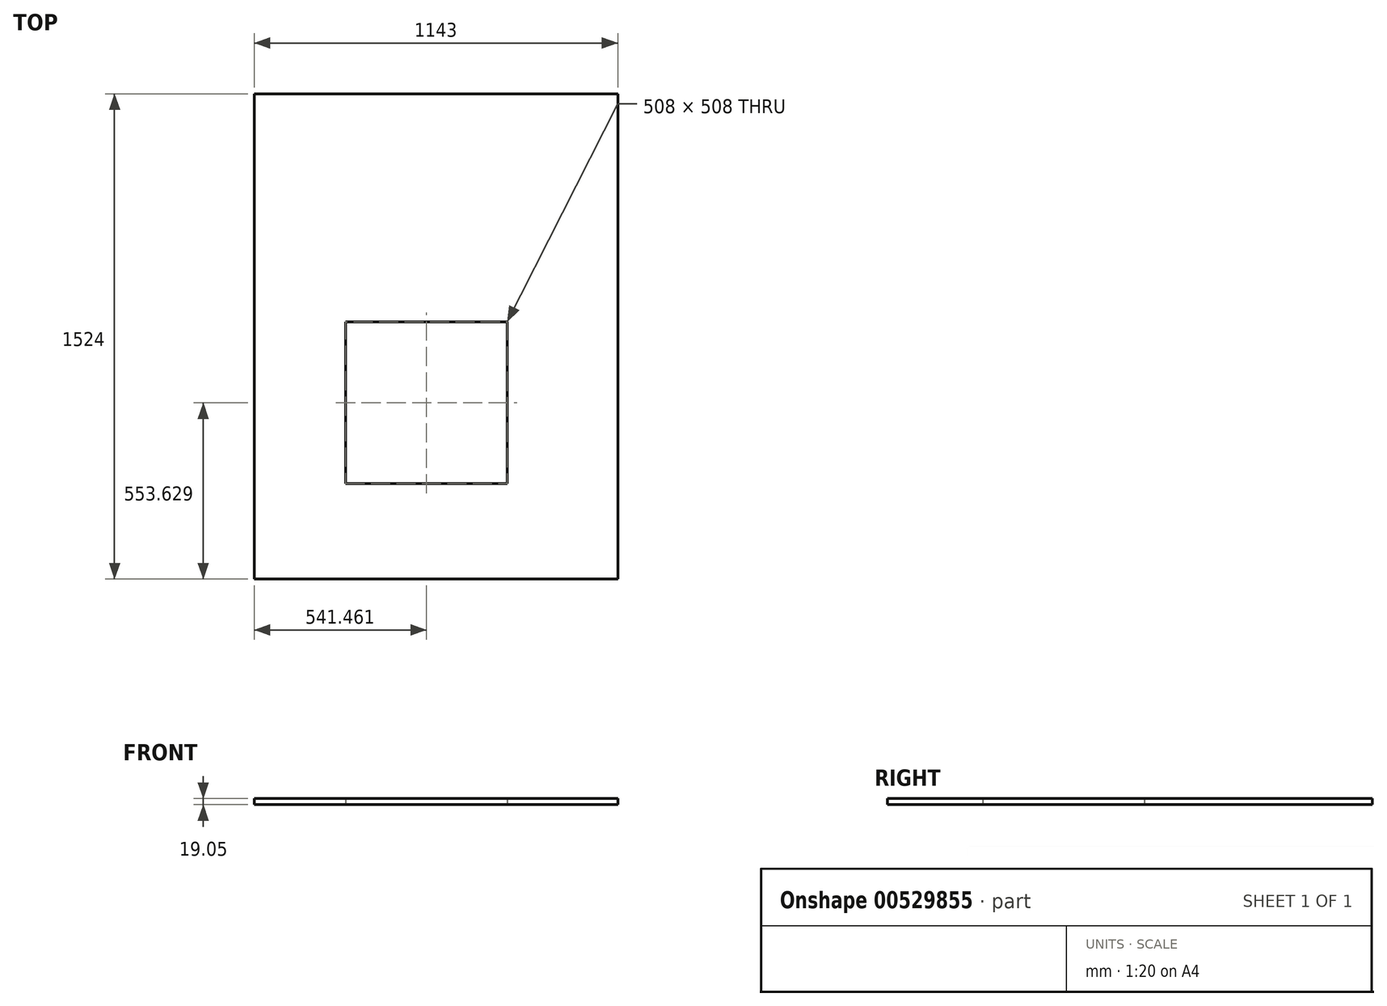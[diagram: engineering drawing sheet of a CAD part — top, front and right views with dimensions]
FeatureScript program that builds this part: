
annotation { "Feature Type Name" : "Feature", "Feature Type Description" : "" }
export const myFeature = defineFeature(function(context is Context, id is Id, definition is map)
    precondition{}
    {
        {
            var Q0;
            Q0=qCreatedBy(makeId("Top.planeOp"),FACE);
            var sketch = newSketch(context, id + "F0", { "sketchPlane" : qUnion([Q0])});
            skLineSegment(sketch, "E0.bottom", {"start": v(-571.59, 1082.27) * mm, "end": v(571.41, 1082.27) * mm});
            skLineSegment(sketch, "E0.top", {"start": v(-571.59, -441.73) * mm, "end": v(571.41, -441.73) * mm});
            skLineSegment(sketch, "E0.left", {"start": v(-571.59, 1082.27) * mm, "end": v(-571.59, -441.73) * mm});
            skLineSegment(sketch, "E0.right", {"start": v(571.41, 1082.27) * mm, "end": v(571.41, -441.73) * mm});
            skLineSegment(sketch, "E1.bottom", {"start": v(-284.13, 365.9) * mm, "end": v(223.87, 365.9) * mm});
            skLineSegment(sketch, "E1.top", {"start": v(-284.13, -142.1) * mm, "end": v(223.87, -142.1) * mm});
            skLineSegment(sketch, "E1.left", {"start": v(-284.13, 365.9) * mm, "end": v(-284.13, -142.1) * mm});
            skLineSegment(sketch, "E1.right", {"start": v(223.87, 365.9) * mm, "end": v(223.87, -142.1) * mm});
            skSolve(sketch);
        }
        {
            var Q0;
            Q0=makeQuery(id+"F0.imprint","IMPRINT",FACE,{"disambiguationData":[TD([[makeQuery(id+"F0.imprint","IMPRINT",EDGE,{"derivedFrom":sQuery(id+"F0.wireOp",EDGE,"E0.bottom")}),-1.0]])]});
            extrude(context, id + "F1", {"entities" : qUnion([Q0]), "depth" : 19.05 * mm, "offsetDistance" : 25.4 * mm});
        }
    });
